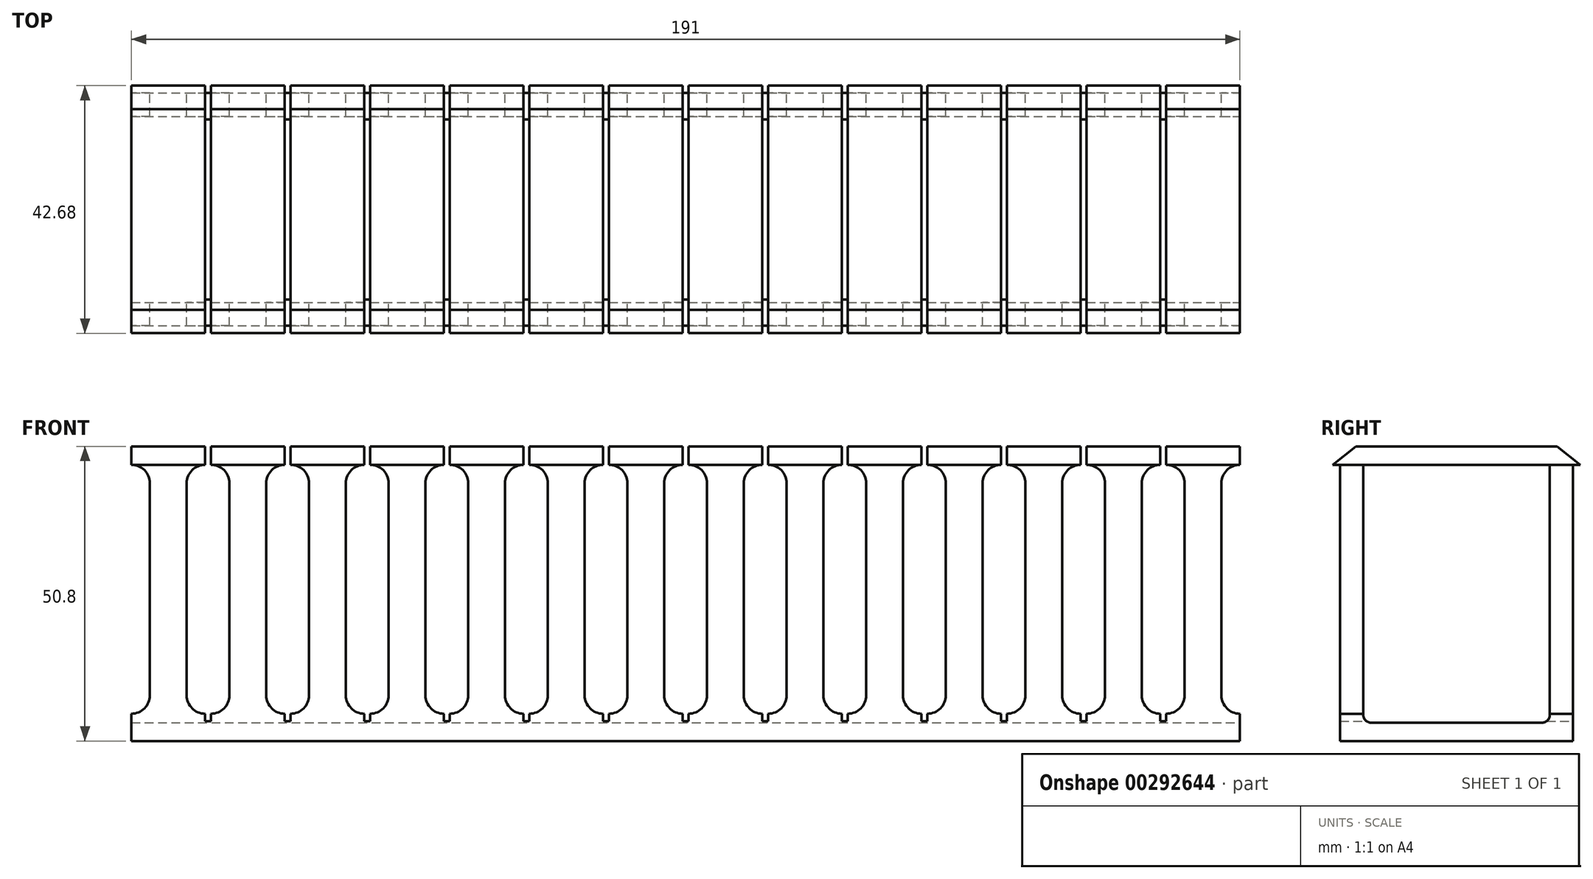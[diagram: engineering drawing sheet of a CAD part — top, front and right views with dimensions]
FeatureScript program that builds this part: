
annotation { "Feature Type Name" : "Feature", "Feature Type Description" : "" }
export const myFeature = defineFeature(function(context is Context, id is Id, definition is map)
    precondition{}
    {
        {
            var Q0;
            Q0=qCreatedBy(makeId("Front.planeOp"),FACE);
            var sketch = newSketch(context, id + "F0", { "sketchPlane" : qUnion([Q0])});
            skLineSegment(sketch, "E0.bottom", {"start": v(-95.5, 0) * mm, "end": v(95.5, 0) * mm});
            skLineSegment(sketch, "E0.top", {"start": v(-95.5, 50.8) * mm, "end": v(-82.8, 50.8) * mm});
            skLineSegment(sketch, "E0.left", {"start": v(-95.5, 0) * mm, "end": v(-95.5, 4.7) * mm});
            skLineSegment(sketch, "E0.right", {"start": v(95.5, 0) * mm, "end": v(95.5, 4.7) * mm});
            skLineSegment(sketch, "E1.trimOffspring", {"start": v(-95.5, 47.63) * mm, "end": v(-95.5, 50.8) * mm});
            skArc(sketch, "E2", {"start": v(-92.33, 44.45) * mm, "mid": v(-93.26, 46.7) * mm, "end": v(-95.5, 47.63) * mm});
            skArc(sketch, "E3", {"start": v(-95.5, 4.7) * mm, "mid": v(-93.26, 5.63) * mm, "end": v(-92.33, 7.87) * mm});
            skLineSegment(sketch, "E4", {"start": v(-92.33, 7.87) * mm, "end": v(-92.33, 44.45) * mm});
            skLineSegment(sketch, "E5", {"start": v(0, 0) * mm, "end": v(0, 0) * mm});
            skLineSegment(sketch, "E6.MirrorCS", {"start": v(95.5, 47.63) * mm, "end": v(95.5, 50.8) * mm});
            skLineSegment(sketch, "E7.MirrorCS", {"start": v(92.33, 7.87) * mm, "end": v(92.33, 44.45) * mm});
            skArc(sketch, "E8.MirrorCS", {"start": v(95.5, 4.7) * mm, "mid": v(93.26, 5.63) * mm, "end": v(92.33, 7.87) * mm});
            skArc(sketch, "E9", {"start": v(95.5, 47.63) * mm, "mid": v(93.26, 46.7) * mm, "end": v(92.33, 44.45) * mm});
            skLineSegment(sketch, "E10", {"start": v(-89.15, 50.8) * mm, "end": v(-89.15, 0) * mm, "construction": true});
            skArc(sketch, "E11.MirrorCS", {"start": v(-85.98, 44.45) * mm, "mid": v(-85.05, 46.7) * mm, "end": v(-82.8, 47.63) * mm});
            skLineSegment(sketch, "E12.MirrorCS", {"start": v(-82.8, 47.63) * mm, "end": v(-82.8, 50.8) * mm});
            skLineSegment(sketch, "E13.MirrorCS", {"start": v(-85.98, 7.87) * mm, "end": v(-85.98, 44.45) * mm});
            skArc(sketch, "E14.MirrorCS", {"start": v(-82.8, 4.7) * mm, "mid": v(-85.05, 5.63) * mm, "end": v(-85.98, 7.87) * mm});
            skLineSegment(sketch, "E15", {"start": v(-81.79, 50.8) * mm, "end": v(-69.09, 50.8) * mm});
            skLineSegment(sketch, "E16", {"start": v(-82.3, 50.8) * mm, "end": v(-82.3, 0) * mm, "construction": true});
            skArc(sketch, "E17.MirrorCS", {"start": v(-78.61, 44.45) * mm, "mid": v(-79.54, 46.7) * mm, "end": v(-81.79, 47.63) * mm});
            skLineSegment(sketch, "E18.MirrorCS", {"start": v(-81.79, 47.63) * mm, "end": v(-81.79, 50.8) * mm});
            skLineSegment(sketch, "E19.MirrorCS", {"start": v(-78.61, 7.87) * mm, "end": v(-78.61, 44.45) * mm});
            skArc(sketch, "E20.MirrorCS", {"start": v(-81.79, 4.7) * mm, "mid": v(-79.54, 5.63) * mm, "end": v(-78.61, 7.87) * mm});
            skLineSegment(sketch, "E21", {"start": v(-75.44, 50.8) * mm, "end": v(-75.44, 0) * mm, "construction": true});
            skLineSegment(sketch, "E22.MirrorCS", {"start": v(-69.09, 47.63) * mm, "end": v(-69.09, 50.8) * mm});
            skArc(sketch, "E23.MirrorCS", {"start": v(-72.26, 44.45) * mm, "mid": v(-71.33, 46.7) * mm, "end": v(-69.09, 47.63) * mm});
            skLineSegment(sketch, "E24.MirrorCS", {"start": v(-72.26, 7.87) * mm, "end": v(-72.26, 44.45) * mm});
            skArc(sketch, "E25.MirrorCS", {"start": v(-69.09, 4.7) * mm, "mid": v(-71.33, 5.63) * mm, "end": v(-72.26, 7.87) * mm});
            skLineSegment(sketch, "E26.MirrorCS", {"start": v(-68.07, 47.63) * mm, "end": v(-68.07, 50.8) * mm});
            skArc(sketch, "E27.MirrorCS", {"start": v(-64.9, 44.45) * mm, "mid": v(-65.83, 46.7) * mm, "end": v(-68.07, 47.63) * mm});
            skArc(sketch, "E28.MirrorCS", {"start": v(-68.07, 4.7) * mm, "mid": v(-65.83, 5.63) * mm, "end": v(-64.9, 7.87) * mm});
            skLineSegment(sketch, "E29.MirrorCS", {"start": v(-64.9, 7.87) * mm, "end": v(-64.9, 44.45) * mm});
            skLineSegment(sketch, "E30.MirrorCS", {"start": v(-58.55, 7.87) * mm, "end": v(-58.55, 44.45) * mm});
            skArc(sketch, "E31.MirrorCS", {"start": v(-58.55, 44.45) * mm, "mid": v(-57.62, 46.7) * mm, "end": v(-55.37, 47.63) * mm});
            skArc(sketch, "E32.MirrorCS", {"start": v(-55.37, 4.7) * mm, "mid": v(-57.62, 5.63) * mm, "end": v(-58.55, 7.87) * mm});
            skLineSegment(sketch, "E33", {"start": v(-68.07, 50.8) * mm, "end": v(-55.37, 50.8) * mm});
            skLineSegment(sketch, "E34", {"start": v(-61.72, 50.8) * mm, "end": v(-61.72, 0) * mm, "construction": true});
            skArc(sketch, "E35.MirrorCS", {"start": v(-51.18, 44.45) * mm, "mid": v(-52.11, 46.7) * mm, "end": v(-54.36, 47.63) * mm});
            skLineSegment(sketch, "E36.MirrorCS", {"start": v(-54.36, 47.63) * mm, "end": v(-54.36, 50.8) * mm});
            skLineSegment(sketch, "E37.MirrorCS", {"start": v(-55.37, 47.63) * mm, "end": v(-55.37, 50.8) * mm});
            skArc(sketch, "E38.MirrorCS", {"start": v(-54.36, 4.7) * mm, "mid": v(-52.11, 5.63) * mm, "end": v(-51.18, 7.87) * mm});
            skLineSegment(sketch, "E39.MirrorCS", {"start": v(-51.18, 7.87) * mm, "end": v(-51.18, 44.45) * mm});
            skLineSegment(sketch, "E40", {"start": v(-54.36, 50.8) * mm, "end": v(-41.66, 50.8) * mm});
            skLineSegment(sketch, "E41", {"start": v(-48, 50.8) * mm, "end": v(-48, 0) * mm, "construction": true});
            skLineSegment(sketch, "E42.MirrorCS", {"start": v(-68.58, 50.8) * mm, "end": v(-68.58, 0) * mm, "construction": true});
            skLineSegment(sketch, "E43.MirrorCS", {"start": v(-54.86, 50.8) * mm, "end": v(-54.86, 0) * mm, "construction": true});
            skLineSegment(sketch, "E44.MirrorCS", {"start": v(-44.83, 7.87) * mm, "end": v(-44.83, 44.45) * mm});
            skArc(sketch, "E45.MirrorCS", {"start": v(-44.83, 44.45) * mm, "mid": v(-43.9, 46.7) * mm, "end": v(-41.66, 47.63) * mm});
            skLineSegment(sketch, "E46.MirrorCS", {"start": v(-41.66, 47.63) * mm, "end": v(-41.66, 50.8) * mm});
            skLineSegment(sketch, "E47.MirrorCS", {"start": v(-41.15, 50.8) * mm, "end": v(-41.15, 0) * mm, "construction": true});
            skArc(sketch, "E48.MirrorCS", {"start": v(-41.66, 4.7) * mm, "mid": v(-43.9, 5.63) * mm, "end": v(-44.83, 7.87) * mm});
            skArc(sketch, "E49.MirrorCS", {"start": v(-37.46, 44.45) * mm, "mid": v(-38.4, 46.7) * mm, "end": v(-40.64, 47.63) * mm});
            skLineSegment(sketch, "E50.MirrorCS", {"start": v(-40.64, 47.63) * mm, "end": v(-40.64, 50.8) * mm});
            skLineSegment(sketch, "E51.MirrorCS", {"start": v(-37.47, 7.87) * mm, "end": v(-37.47, 44.45) * mm});
            skArc(sketch, "E52.MirrorCS", {"start": v(-40.64, 4.7) * mm, "mid": v(-38.4, 5.63) * mm, "end": v(-37.47, 7.87) * mm});
            skLineSegment(sketch, "E53.MirrorCS", {"start": v(-34.29, 50.8) * mm, "end": v(-34.3, 0) * mm, "construction": true});
            skLineSegment(sketch, "E54", {"start": v(-40.64, 50.8) * mm, "end": v(-27.94, 50.8) * mm});
            skLineSegment(sketch, "E55.MirrorCS", {"start": v(-27.94, 47.62) * mm, "end": v(-27.94, 50.8) * mm});
            skArc(sketch, "E56.MirrorCS", {"start": v(-31.12, 44.45) * mm, "mid": v(-30.19, 46.7) * mm, "end": v(-27.94, 47.62) * mm});
            skLineSegment(sketch, "E57.MirrorCS", {"start": v(-31.12, 7.87) * mm, "end": v(-31.11, 44.45) * mm});
            skArc(sketch, "E58.MirrorCS", {"start": v(-27.94, 4.7) * mm, "mid": v(-30.19, 5.63) * mm, "end": v(-31.11, 7.87) * mm});
            skLineSegment(sketch, "E59.MirrorCS", {"start": v(-27.43, 50.8) * mm, "end": v(-27.43, 0) * mm, "construction": true});
            skLineSegment(sketch, "E60.MirrorCS", {"start": v(-26.92, 47.62) * mm, "end": v(-26.92, 50.8) * mm});
            skArc(sketch, "E61.MirrorCS", {"start": v(-23.75, 44.45) * mm, "mid": v(-24.68, 46.7) * mm, "end": v(-26.92, 47.62) * mm});
            skLineSegment(sketch, "E62.MirrorCS", {"start": v(-23.75, 7.87) * mm, "end": v(-23.75, 44.45) * mm});
            skArc(sketch, "E63.MirrorCS", {"start": v(-26.92, 4.7) * mm, "mid": v(-24.68, 5.63) * mm, "end": v(-23.75, 7.87) * mm});
            skLineSegment(sketch, "E64", {"start": v(-26.92, 50.8) * mm, "end": v(-14.22, 50.8) * mm});
            skLineSegment(sketch, "E65", {"start": v(-20.57, 50.8) * mm, "end": v(-20.57, 0) * mm, "construction": true});
            skArc(sketch, "E66.MirrorCS", {"start": v(-17.4, 44.45) * mm, "mid": v(-16.47, 46.7) * mm, "end": v(-14.22, 47.62) * mm});
            skLineSegment(sketch, "E67.MirrorCS", {"start": v(-14.22, 47.62) * mm, "end": v(-14.22, 50.8) * mm});
            skLineSegment(sketch, "E68.MirrorCS", {"start": v(-17.4, 7.87) * mm, "end": v(-17.4, 44.45) * mm});
            skArc(sketch, "E69.MirrorCS", {"start": v(-14.22, 4.7) * mm, "mid": v(-16.47, 5.63) * mm, "end": v(-17.4, 7.87) * mm});
            skLineSegment(sketch, "E70.MirrorCS", {"start": v(-13.2, 47.62) * mm, "end": v(-13.2, 50.8) * mm});
            skArc(sketch, "E71.MirrorCS", {"start": v(-10.03, 44.45) * mm, "mid": v(-10.96, 46.7) * mm, "end": v(-13.2, 47.62) * mm});
            skLineSegment(sketch, "E72.MirrorCS", {"start": v(-10.03, 7.87) * mm, "end": v(-10.03, 44.45) * mm});
            skArc(sketch, "E73.MirrorCS", {"start": v(-13.2, 4.7) * mm, "mid": v(-10.96, 5.63) * mm, "end": v(-10.03, 7.87) * mm});
            skLineSegment(sketch, "E74.MirrorCS", {"start": v(-13.72, 50.8) * mm, "end": v(-13.72, 0) * mm, "construction": true});
            skLineSegment(sketch, "E75", {"start": v(-13.2, 50.8) * mm, "end": v(-0.5, 50.8) * mm});
            skLineSegment(sketch, "E76", {"start": v(-6.86, 50.8) * mm, "end": v(-6.86, 0) * mm, "construction": true});
            skArc(sketch, "E77.MirrorCS", {"start": v(-3.68, 44.45) * mm, "mid": v(-2.75, 46.7) * mm, "end": v(-0.5, 47.62) * mm});
            skLineSegment(sketch, "E78.MirrorCS", {"start": v(-3.68, 7.87) * mm, "end": v(-3.68, 44.45) * mm});
            skLineSegment(sketch, "E79.MirrorCS", {"start": v(-0.5, 47.62) * mm, "end": v(-0.5, 50.8) * mm});
            skArc(sketch, "E80.MirrorCS", {"start": v(-0.5, 4.7) * mm, "mid": v(-2.75, 5.63) * mm, "end": v(-3.68, 7.87) * mm});
            skLineSegment(sketch, "E81.MirrorCS", {"start": v(3.68, 7.87) * mm, "end": v(3.68, 44.45) * mm});
            skArc(sketch, "E82.MirrorCS", {"start": v(0.5, 4.7) * mm, "mid": v(2.75, 5.63) * mm, "end": v(3.68, 7.87) * mm});
            skArc(sketch, "E83.MirrorCS", {"start": v(3.68, 44.45) * mm, "mid": v(2.75, 46.7) * mm, "end": v(0.5, 47.62) * mm});
            skLineSegment(sketch, "E84.MirrorCS", {"start": v(0.5, 47.62) * mm, "end": v(0.5, 50.8) * mm});
            skLineSegment(sketch, "E85.MirrorCS", {"start": v(0, 50.8) * mm, "end": v(0, 0) * mm, "construction": true});
            skLineSegment(sketch, "E86", {"start": v(0.5, 50.8) * mm, "end": v(13.2, 50.8) * mm});
            skLineSegment(sketch, "E87", {"start": v(6.86, 50.8) * mm, "end": v(6.86, 0) * mm, "construction": true});
            skArc(sketch, "E88.MirrorCS", {"start": v(10.03, 44.45) * mm, "mid": v(10.96, 46.7) * mm, "end": v(13.2, 47.62) * mm});
            skLineSegment(sketch, "E89.MirrorCS", {"start": v(13.2, 47.62) * mm, "end": v(13.2, 50.8) * mm});
            skArc(sketch, "E90.MirrorCS", {"start": v(13.2, 4.7) * mm, "mid": v(10.96, 5.63) * mm, "end": v(10.03, 7.87) * mm});
            skLineSegment(sketch, "E91.MirrorCS", {"start": v(13.72, 50.8) * mm, "end": v(13.72, 0) * mm, "construction": true});
            skLineSegment(sketch, "E92.MirrorCS", {"start": v(17.4, 7.87) * mm, "end": v(17.4, 44.45) * mm});
            skArc(sketch, "E93.MirrorCS", {"start": v(14.22, 4.7) * mm, "mid": v(16.47, 5.63) * mm, "end": v(17.4, 7.87) * mm});
            skArc(sketch, "E94.MirrorCS", {"start": v(17.4, 44.45) * mm, "mid": v(16.47, 46.7) * mm, "end": v(14.22, 47.62) * mm});
            skLineSegment(sketch, "E95.MirrorCS", {"start": v(10.03, 7.87) * mm, "end": v(10.03, 44.45) * mm});
            skLineSegment(sketch, "E96.MirrorCS", {"start": v(14.22, 47.62) * mm, "end": v(14.22, 50.8) * mm});
            skLineSegment(sketch, "E97", {"start": v(14.22, 50.8) * mm, "end": v(26.92, 50.8) * mm});
            skLineSegment(sketch, "E98", {"start": v(20.57, 50.8) * mm, "end": v(20.57, 0) * mm, "construction": true});
            skArc(sketch, "E99.MirrorCS", {"start": v(26.92, 4.7) * mm, "mid": v(24.68, 5.63) * mm, "end": v(23.75, 7.87) * mm});
            skArc(sketch, "E100.MirrorCS", {"start": v(27.94, 4.7) * mm, "mid": v(30.19, 5.63) * mm, "end": v(31.11, 7.87) * mm});
            skLineSegment(sketch, "E101.MirrorCS", {"start": v(31.11, 7.87) * mm, "end": v(31.11, 44.45) * mm});
            skLineSegment(sketch, "E102.MirrorCS", {"start": v(27.43, 50.8) * mm, "end": v(27.43, 0) * mm, "construction": true});
            skLineSegment(sketch, "E103.MirrorCS", {"start": v(23.75, 7.87) * mm, "end": v(23.75, 44.45) * mm});
            skArc(sketch, "E104.MirrorCS", {"start": v(23.75, 44.45) * mm, "mid": v(24.68, 46.7) * mm, "end": v(26.92, 47.62) * mm});
            skLineSegment(sketch, "E105.MirrorCS", {"start": v(26.92, 47.62) * mm, "end": v(26.92, 50.8) * mm});
            skLineSegment(sketch, "E106.MirrorCS", {"start": v(27.94, 47.62) * mm, "end": v(27.94, 50.8) * mm});
            skArc(sketch, "E107.MirrorCS", {"start": v(31.11, 44.45) * mm, "mid": v(30.19, 46.7) * mm, "end": v(27.94, 47.62) * mm});
            skLineSegment(sketch, "E108", {"start": v(27.94, 50.8) * mm, "end": v(40.64, 50.8) * mm});
            skLineSegment(sketch, "E109", {"start": v(34.29, 50.8) * mm, "end": v(34.29, 0) * mm, "construction": true});
            skArc(sketch, "E110.MirrorCS", {"start": v(40.64, 4.7) * mm, "mid": v(38.4, 5.63) * mm, "end": v(37.47, 7.87) * mm});
            skLineSegment(sketch, "E111.MirrorCS", {"start": v(37.47, 7.87) * mm, "end": v(37.47, 44.45) * mm});
            skArc(sketch, "E112.MirrorCS", {"start": v(37.46, 44.45) * mm, "mid": v(38.4, 46.7) * mm, "end": v(40.64, 47.62) * mm});
            skLineSegment(sketch, "E113.MirrorCS", {"start": v(40.64, 47.62) * mm, "end": v(40.64, 50.8) * mm});
            skLineSegment(sketch, "E114.MirrorCS", {"start": v(41.15, 50.8) * mm, "end": v(41.15, 0) * mm, "construction": true});
            skLineSegment(sketch, "E115.MirrorCS", {"start": v(41.66, 47.62) * mm, "end": v(41.66, 50.8) * mm});
            skArc(sketch, "E116.MirrorCS", {"start": v(44.83, 44.45) * mm, "mid": v(43.9, 46.7) * mm, "end": v(41.66, 47.62) * mm});
            skLineSegment(sketch, "E117.MirrorCS", {"start": v(44.83, 7.87) * mm, "end": v(44.83, 44.45) * mm});
            skArc(sketch, "E118.MirrorCS", {"start": v(41.66, 4.7) * mm, "mid": v(43.9, 5.63) * mm, "end": v(44.83, 7.87) * mm});
            skLineSegment(sketch, "E119", {"start": v(41.66, 50.8) * mm, "end": v(54.36, 50.8) * mm});
            skLineSegment(sketch, "E120", {"start": v(48, 50.8) * mm, "end": v(48, 0) * mm, "construction": true});
            skLineSegment(sketch, "E121.MirrorCS", {"start": v(51.18, 7.87) * mm, "end": v(51.18, 44.45) * mm});
            skArc(sketch, "E122.MirrorCS", {"start": v(51.18, 44.45) * mm, "mid": v(52.11, 46.7) * mm, "end": v(54.36, 47.62) * mm});
            skLineSegment(sketch, "E123.MirrorCS", {"start": v(54.36, 47.62) * mm, "end": v(54.36, 50.8) * mm});
            skLineSegment(sketch, "E124.MirrorCS", {"start": v(54.86, 50.8) * mm, "end": v(54.86, 0) * mm, "construction": true});
            skLineSegment(sketch, "E125.MirrorCS", {"start": v(55.37, 47.62) * mm, "end": v(55.37, 50.8) * mm});
            skArc(sketch, "E126.MirrorCS", {"start": v(58.55, 44.45) * mm, "mid": v(57.62, 46.7) * mm, "end": v(55.37, 47.62) * mm});
            skLineSegment(sketch, "E127.MirrorCS", {"start": v(58.55, 7.87) * mm, "end": v(58.55, 44.45) * mm});
            skArc(sketch, "E128.MirrorCS", {"start": v(55.37, 4.7) * mm, "mid": v(57.62, 5.63) * mm, "end": v(58.55, 7.87) * mm});
            skArc(sketch, "E129.MirrorCS", {"start": v(54.36, 4.7) * mm, "mid": v(52.11, 5.63) * mm, "end": v(51.18, 7.87) * mm});
            skLineSegment(sketch, "E130", {"start": v(55.37, 50.8) * mm, "end": v(68.07, 50.8) * mm});
            skLineSegment(sketch, "E131", {"start": v(61.72, 50.8) * mm, "end": v(61.72, 0) * mm, "construction": true});
            skLineSegment(sketch, "E132.MirrorCS", {"start": v(64.9, 7.87) * mm, "end": v(64.9, 44.45) * mm});
            skArc(sketch, "E133.MirrorCS", {"start": v(64.9, 44.45) * mm, "mid": v(65.83, 46.7) * mm, "end": v(68.07, 47.63) * mm});
            skLineSegment(sketch, "E134.MirrorCS", {"start": v(68.07, 47.63) * mm, "end": v(68.07, 50.8) * mm});
            skArc(sketch, "E135.MirrorCS", {"start": v(68.07, 4.7) * mm, "mid": v(65.83, 5.63) * mm, "end": v(64.9, 7.87) * mm});
            skLineSegment(sketch, "E136.MirrorCS", {"start": v(68.58, 50.8) * mm, "end": v(68.58, 0) * mm, "construction": true});
            skLineSegment(sketch, "E137.MirrorCS", {"start": v(72.26, 7.87) * mm, "end": v(72.26, 44.45) * mm});
            skArc(sketch, "E138.MirrorCS", {"start": v(69.09, 4.7) * mm, "mid": v(71.33, 5.63) * mm, "end": v(72.26, 7.87) * mm});
            skArc(sketch, "E139.MirrorCS", {"start": v(72.26, 44.45) * mm, "mid": v(71.33, 46.7) * mm, "end": v(69.09, 47.63) * mm});
            skLineSegment(sketch, "E140.MirrorCS", {"start": v(69.09, 47.63) * mm, "end": v(69.09, 50.8) * mm});
            skLineSegment(sketch, "E141", {"start": v(69.09, 50.8) * mm, "end": v(81.79, 50.8) * mm});
            skLineSegment(sketch, "E142", {"start": v(75.44, 50.8) * mm, "end": v(75.44, 0) * mm, "construction": true});
            skLineSegment(sketch, "E143.MirrorCS", {"start": v(78.61, 7.87) * mm, "end": v(78.61, 44.45) * mm});
            skArc(sketch, "E144.MirrorCS", {"start": v(78.61, 44.45) * mm, "mid": v(79.54, 46.7) * mm, "end": v(81.79, 47.63) * mm});
            skLineSegment(sketch, "E145.MirrorCS", {"start": v(81.79, 47.63) * mm, "end": v(81.79, 50.8) * mm});
            skArc(sketch, "E146.MirrorCS", {"start": v(81.79, 4.7) * mm, "mid": v(79.54, 5.63) * mm, "end": v(78.61, 7.87) * mm});
            skLineSegment(sketch, "E147.MirrorCS", {"start": v(82.3, 50.8) * mm, "end": v(82.3, 0) * mm, "construction": true});
            skLineSegment(sketch, "E148.MirrorCS", {"start": v(85.98, 7.87) * mm, "end": v(85.98, 44.45) * mm});
            skArc(sketch, "E149.MirrorCS", {"start": v(82.8, 4.7) * mm, "mid": v(85.05, 5.63) * mm, "end": v(85.98, 7.87) * mm});
            skArc(sketch, "E150.MirrorCS", {"start": v(85.98, 44.45) * mm, "mid": v(85.05, 46.7) * mm, "end": v(82.8, 47.63) * mm});
            skLineSegment(sketch, "E151.MirrorCS", {"start": v(82.8, 47.63) * mm, "end": v(82.8, 50.8) * mm});
            skLineSegment(sketch, "E152", {"start": v(-0.5, 4.7) * mm, "end": v(-0.5, 3.43) * mm});
            skLineSegment(sketch, "E153", {"start": v(-0.5, 3.43) * mm, "end": v(0.5, 3.43) * mm});
            skLineSegment(sketch, "E154", {"start": v(0.5, 3.43) * mm, "end": v(0.5, 4.7) * mm});
            skLineSegment(sketch, "E155.MirrorCS", {"start": v(13.2, 3.43) * mm, "end": v(13.2, 4.7) * mm});
            skLineSegment(sketch, "E156.MirrorCS", {"start": v(14.22, 3.43) * mm, "end": v(13.2, 3.43) * mm});
            skLineSegment(sketch, "E157.MirrorCS", {"start": v(14.22, 4.7) * mm, "end": v(14.22, 3.43) * mm});
            skLineSegment(sketch, "E158.MirrorCS", {"start": v(26.92, 3.43) * mm, "end": v(27.94, 3.43) * mm});
            skLineSegment(sketch, "E159.MirrorCS", {"start": v(26.92, 4.7) * mm, "end": v(26.92, 3.43) * mm});
            skLineSegment(sketch, "E160.MirrorCS", {"start": v(27.94, 3.43) * mm, "end": v(27.94, 4.7) * mm});
            skLineSegment(sketch, "E161.MirrorCS", {"start": v(55.37, 3.43) * mm, "end": v(54.36, 3.43) * mm});
            skLineSegment(sketch, "E162.MirrorCS", {"start": v(54.36, 3.43) * mm, "end": v(54.36, 4.7) * mm});
            skLineSegment(sketch, "E163.MirrorCS", {"start": v(55.37, 4.7) * mm, "end": v(55.37, 3.43) * mm});
            skLineSegment(sketch, "E164.MirrorCS", {"start": v(41.66, 4.7) * mm, "end": v(41.66, 3.43) * mm});
            skLineSegment(sketch, "E165.MirrorCS", {"start": v(40.64, 3.43) * mm, "end": v(40.64, 4.7) * mm});
            skLineSegment(sketch, "E166.MirrorCS", {"start": v(41.66, 3.43) * mm, "end": v(40.64, 3.43) * mm});
            skLineSegment(sketch, "E167.MirrorCS", {"start": v(68.07, 4.7) * mm, "end": v(68.07, 3.43) * mm});
            skLineSegment(sketch, "E168.MirrorCS", {"start": v(68.07, 3.43) * mm, "end": v(69.09, 3.43) * mm});
            skLineSegment(sketch, "E169.MirrorCS", {"start": v(69.09, 3.43) * mm, "end": v(69.09, 4.7) * mm});
            skLineSegment(sketch, "E170.MirrorCS", {"start": v(81.79, 3.43) * mm, "end": v(81.79, 4.7) * mm});
            skLineSegment(sketch, "E171.MirrorCS", {"start": v(82.8, 3.43) * mm, "end": v(81.79, 3.43) * mm});
            skLineSegment(sketch, "E172.MirrorCS", {"start": v(82.8, 4.7) * mm, "end": v(82.8, 3.43) * mm});
            skLineSegment(sketch, "E173.MirrorCS", {"start": v(-14.22, 3.43) * mm, "end": v(-14.22, 4.7) * mm});
            skLineSegment(sketch, "E174.MirrorCS", {"start": v(-13.2, 3.43) * mm, "end": v(-14.22, 3.43) * mm});
            skLineSegment(sketch, "E175.MirrorCS", {"start": v(-13.2, 4.7) * mm, "end": v(-13.2, 3.43) * mm});
            skLineSegment(sketch, "E176.MirrorCS", {"start": v(-26.92, 3.43) * mm, "end": v(-26.92, 4.7) * mm});
            skLineSegment(sketch, "E177.MirrorCS", {"start": v(-27.94, 4.7) * mm, "end": v(-27.94, 3.43) * mm});
            skLineSegment(sketch, "E178.MirrorCS", {"start": v(-27.94, 3.43) * mm, "end": v(-26.92, 3.43) * mm});
            skLineSegment(sketch, "E179.MirrorCS", {"start": v(-41.66, 3.43) * mm, "end": v(-41.66, 4.7) * mm});
            skLineSegment(sketch, "E180.MirrorCS", {"start": v(-40.64, 3.43) * mm, "end": v(-41.66, 3.43) * mm});
            skLineSegment(sketch, "E181.MirrorCS", {"start": v(-40.64, 4.7) * mm, "end": v(-40.64, 3.43) * mm});
            skLineSegment(sketch, "E182.MirrorCS", {"start": v(-54.36, 3.43) * mm, "end": v(-54.36, 4.7) * mm});
            skLineSegment(sketch, "E183", {"start": v(-55.37, 4.7) * mm, "end": v(-55.37, 3.43) * mm});
            skLineSegment(sketch, "E184", {"start": v(-55.37, 3.43) * mm, "end": v(-54.36, 3.43) * mm});
            skLineSegment(sketch, "E185.MirrorCS", {"start": v(-69.09, 3.43) * mm, "end": v(-69.09, 4.7) * mm});
            skLineSegment(sketch, "E186.MirrorCS", {"start": v(-68.07, 3.43) * mm, "end": v(-69.09, 3.43) * mm});
            skLineSegment(sketch, "E187.MirrorCS", {"start": v(-68.07, 4.7) * mm, "end": v(-68.07, 3.43) * mm});
            skLineSegment(sketch, "E188.MirrorCS", {"start": v(-81.79, 3.43) * mm, "end": v(-81.79, 4.7) * mm});
            skLineSegment(sketch, "E189.MirrorCS", {"start": v(-82.8, 4.7) * mm, "end": v(-82.8, 3.43) * mm});
            skLineSegment(sketch, "E190.MirrorCS", {"start": v(-82.8, 3.43) * mm, "end": v(-81.79, 3.43) * mm});
            skLineSegment(sketch, "E191.trimOffspring", {"start": v(-54.36, 50.8) * mm, "end": v(-48, 50.8) * mm});
            skLineSegment(sketch, "E192.trimOffspring", {"start": v(82.8, 50.8) * mm, "end": v(95.5, 50.8) * mm});
            skLineSegment(sketch, "E193.trimOffspring", {"start": v(41.15, 50.8) * mm, "end": v(48, 50.8) * mm});
            skLineSegment(sketch, "E194.trimOffspring", {"start": v(27.94, 50.8) * mm, "end": v(34.29, 50.8) * mm});
            skSolve(sketch);
        }
        {
            var Q0;
            Q0 = qSketchRegion(id + "F0", true);
            extrude(context, id + "F1", {"entities" : qUnion([Q0]), "depth" : 42.67 * mm, "symmetric" : true});
        }
        {
            var Q0;
            Q0=makeQuery(id+"F1.opExtrude","SWEPT_FACE",FACE,{"disambiguationData":[OSD([sQuery(id+"F0.wireOp",EDGE,"E6.MirrorCS")])]});
            var sketch = newSketch(context, id + "F2", { "sketchPlane" : qUnion([Q0])});
            skLineSegment(sketch, "E195", {"start": v(-21.34, 50.8) * mm, "end": v(21.34, 50.8) * mm});
            skLineSegment(sketch, "E196", {"start": v(21.34, 50.8) * mm, "end": v(21.34, 0) * mm});
            skLineSegment(sketch, "E197", {"start": v(21.34, 0) * mm, "end": v(-21.34, 0) * mm});
            skLineSegment(sketch, "E198", {"start": v(-21.34, 0) * mm, "end": v(-21.34, 50.8) * mm});
            skLineSegment(sketch, "E199", {"start": v(21.34, 50.8) * mm, "end": v(18.7, 50.8) * mm});
            skLineSegment(sketch, "E200", {"start": v(0, 55.4) * mm, "end": v(0, -7.26) * mm, "construction": true});
            skLineSegment(sketch, "E201.MirrorCS", {"start": v(-21.34, 50.8) * mm, "end": v(-18.7, 50.8) * mm});
            skLineSegment(sketch, "E202", {"start": v(24.79, 0) * mm, "end": v(24.79, 3.18) * mm});
            skLineSegment(sketch, "E203", {"start": v(16.05, 50.8) * mm, "end": v(16.05, 3.18) * mm});
            skLineSegment(sketch, "E204", {"start": v(16.05, 3.18) * mm, "end": v(-16.05, 3.17) * mm});
            skLineSegment(sketch, "E205", {"start": v(-16.05, 3.17) * mm, "end": v(-16.05, 50.8) * mm});
            skLineSegment(sketch, "E206", {"start": v(-16.05, 50.8) * mm, "end": v(16.05, 50.8) * mm});
            skSolve(sketch);
        }
        {
            var Q0;
            {var subQ0=sQuery(id+"F2.wireOp",EDGE,"E204");Q0=makeQuery(id+"F2.imprint","IMPRINT",FACE,{"disambiguationData":[TD([[makeQuery(id+"F2.imprint","IMPRINT",EDGE,{"derivedFrom":subQ0}),-1.0]])]});}
            var Q1;
            {var subQ0=sQuery(id+"F2.wireOp",EDGE,"E206");Q1=makeQuery(id+"F2.imprint","IMPRINT",FACE,{"disambiguationData":[TD([[makeQuery(id+"F2.imprint","IMPRINT",EDGE,{"derivedFrom":subQ0}),-1.0]])]});}
            extrude(context, id + "F3", {"entities" : qUnion([Q0, Q1]), "operationType" : NewBodyOperationType.REMOVE, "endBound" : BoundingType.THROUGH_ALL, "oppositeDirection" : true, "depth" : 25.4 * mm});
        }
        {
            var Q0;
            Q0=qCreatedBy(makeId("Right.planeOp"),FACE);
            var sketch = newSketch(context, id + "F4", { "sketchPlane" : qUnion([Q0])});
            skLineSegment(sketch, "E207", {"start": v(0, -5.93) * mm, "end": v(0, 55.46) * mm, "construction": true});
            skSolve(sketch);
        }
        {
            var Q0;
            {var subQ0=sQuery(id+"F2.wireOp",EDGE,"E203");Q0=makeQuery(id+"F3.boolean.opBoolean","COPY",EDGE,{"disambiguationData":[topologyDisambiguationEdgeConnected([makeQuery(id+"F1.opExtrude","SWEPT_FACE",FACE,{"disambiguationData":[OSD([sQuery(id+"F0.wireOp",EDGE,"E0.top")])]})])],"derivedFrom":makeQuery(id+"F3.opExtrude","SWEPT_EDGE",EDGE,{"disambiguationData":[OSD([sQuery(id+"F2.wireOp",EDGE,"E195"),subQ0,sQuery(id+"F2.wireOp",EDGE,"E206")])]})});}
            var Q1;
            {var subQ0=sQuery(id+"F2.wireOp",EDGE,"E203");Q1=makeQuery(id+"F3.boolean.opBoolean","COPY",EDGE,{"disambiguationData":[topologyDisambiguationEdgeConnected([makeQuery(id+"F1.opExtrude","SWEPT_FACE",FACE,{"disambiguationData":[OSD([sQuery(id+"F0.wireOp",EDGE,"E15")])]})])],"derivedFrom":makeQuery(id+"F3.opExtrude","SWEPT_EDGE",EDGE,{"disambiguationData":[OSD([sQuery(id+"F2.wireOp",EDGE,"E195"),subQ0,sQuery(id+"F2.wireOp",EDGE,"E206")])]})});}
            var Q2;
            {var subQ0=sQuery(id+"F2.wireOp",EDGE,"E203");Q2=makeQuery(id+"F3.boolean.opBoolean","COPY",EDGE,{"disambiguationData":[topologyDisambiguationEdgeConnected([makeQuery(id+"F1.opExtrude","SWEPT_FACE",FACE,{"disambiguationData":[OSD([sQuery(id+"F0.wireOp",EDGE,"E33")])]})])],"derivedFrom":makeQuery(id+"F3.opExtrude","SWEPT_EDGE",EDGE,{"disambiguationData":[OSD([sQuery(id+"F2.wireOp",EDGE,"E195"),subQ0,sQuery(id+"F2.wireOp",EDGE,"E206")])]})});}
            var Q3;
            {var subQ0=sQuery(id+"F2.wireOp",EDGE,"E203");Q3=makeQuery(id+"F3.boolean.opBoolean","COPY",EDGE,{"disambiguationData":[topologyDisambiguationEdgeConnected([makeQuery(id+"F1.opExtrude","SWEPT_FACE",FACE,{"disambiguationData":[OSD([sQuery(id+"F0.wireOp",EDGE,"E40"),sQuery(id+"F0.wireOp",EDGE,"E191.trimOffspring")])]})])],"derivedFrom":makeQuery(id+"F3.opExtrude","SWEPT_EDGE",EDGE,{"disambiguationData":[OSD([sQuery(id+"F2.wireOp",EDGE,"E195"),subQ0,sQuery(id+"F2.wireOp",EDGE,"E206")])]})});}
            var Q4;
            {var subQ0=sQuery(id+"F2.wireOp",EDGE,"E203");Q4=makeQuery(id+"F3.boolean.opBoolean","COPY",EDGE,{"disambiguationData":[topologyDisambiguationEdgeConnected([makeQuery(id+"F1.opExtrude","SWEPT_FACE",FACE,{"disambiguationData":[OSD([sQuery(id+"F0.wireOp",EDGE,"E54")])]})])],"derivedFrom":makeQuery(id+"F3.opExtrude","SWEPT_EDGE",EDGE,{"disambiguationData":[OSD([sQuery(id+"F2.wireOp",EDGE,"E195"),subQ0,sQuery(id+"F2.wireOp",EDGE,"E206")])]})});}
            var Q5;
            {var subQ0=sQuery(id+"F2.wireOp",EDGE,"E203");Q5=makeQuery(id+"F3.boolean.opBoolean","COPY",EDGE,{"disambiguationData":[topologyDisambiguationEdgeConnected([makeQuery(id+"F1.opExtrude","SWEPT_FACE",FACE,{"disambiguationData":[OSD([sQuery(id+"F0.wireOp",EDGE,"E75")])]})])],"derivedFrom":makeQuery(id+"F3.opExtrude","SWEPT_EDGE",EDGE,{"disambiguationData":[OSD([sQuery(id+"F2.wireOp",EDGE,"E195"),subQ0,sQuery(id+"F2.wireOp",EDGE,"E206")])]})});}
            var Q6;
            {var subQ0=sQuery(id+"F2.wireOp",EDGE,"E203");Q6=makeQuery(id+"F3.boolean.opBoolean","COPY",EDGE,{"disambiguationData":[topologyDisambiguationEdgeConnected([makeQuery(id+"F1.opExtrude","SWEPT_FACE",FACE,{"disambiguationData":[OSD([sQuery(id+"F0.wireOp",EDGE,"E86")])]})])],"derivedFrom":makeQuery(id+"F3.opExtrude","SWEPT_EDGE",EDGE,{"disambiguationData":[OSD([sQuery(id+"F2.wireOp",EDGE,"E195"),subQ0,sQuery(id+"F2.wireOp",EDGE,"E206")])]})});}
            var Q7;
            {var subQ0=sQuery(id+"F2.wireOp",EDGE,"E203");Q7=makeQuery(id+"F3.boolean.opBoolean","COPY",EDGE,{"disambiguationData":[topologyDisambiguationEdgeConnected([makeQuery(id+"F1.opExtrude","SWEPT_FACE",FACE,{"disambiguationData":[OSD([sQuery(id+"F0.wireOp",EDGE,"E97")])]})])],"derivedFrom":makeQuery(id+"F3.opExtrude","SWEPT_EDGE",EDGE,{"disambiguationData":[OSD([sQuery(id+"F2.wireOp",EDGE,"E195"),subQ0,sQuery(id+"F2.wireOp",EDGE,"E206")])]})});}
            var Q8;
            {var subQ0=sQuery(id+"F2.wireOp",EDGE,"E203");Q8=makeQuery(id+"F3.boolean.opBoolean","COPY",EDGE,{"disambiguationData":[topologyDisambiguationEdgeConnected([makeQuery(id+"F1.opExtrude","SWEPT_FACE",FACE,{"disambiguationData":[OSD([sQuery(id+"F0.wireOp",EDGE,"E108"),sQuery(id+"F0.wireOp",EDGE,"E194.trimOffspring")])]})])],"derivedFrom":makeQuery(id+"F3.opExtrude","SWEPT_EDGE",EDGE,{"disambiguationData":[OSD([sQuery(id+"F2.wireOp",EDGE,"E195"),subQ0,sQuery(id+"F2.wireOp",EDGE,"E206")])]})});}
            var Q9;
            {var subQ0=sQuery(id+"F2.wireOp",EDGE,"E203");Q9=makeQuery(id+"F3.boolean.opBoolean","COPY",EDGE,{"disambiguationData":[topologyDisambiguationEdgeConnected([makeQuery(id+"F1.opExtrude","SWEPT_FACE",FACE,{"disambiguationData":[OSD([sQuery(id+"F0.wireOp",EDGE,"E119"),sQuery(id+"F0.wireOp",EDGE,"E193.trimOffspring")])]})])],"derivedFrom":makeQuery(id+"F3.opExtrude","SWEPT_EDGE",EDGE,{"disambiguationData":[OSD([sQuery(id+"F2.wireOp",EDGE,"E195"),subQ0,sQuery(id+"F2.wireOp",EDGE,"E206")])]})});}
            var Q10;
            {var subQ0=sQuery(id+"F2.wireOp",EDGE,"E203");Q10=makeQuery(id+"F3.boolean.opBoolean","COPY",EDGE,{"disambiguationData":[topologyDisambiguationEdgeConnected([makeQuery(id+"F1.opExtrude","SWEPT_FACE",FACE,{"disambiguationData":[OSD([sQuery(id+"F0.wireOp",EDGE,"E130")])]})])],"derivedFrom":makeQuery(id+"F3.opExtrude","SWEPT_EDGE",EDGE,{"disambiguationData":[OSD([sQuery(id+"F2.wireOp",EDGE,"E195"),subQ0,sQuery(id+"F2.wireOp",EDGE,"E206")])]})});}
            var Q11;
            {var subQ0=sQuery(id+"F2.wireOp",EDGE,"E203");Q11=makeQuery(id+"F3.boolean.opBoolean","COPY",EDGE,{"disambiguationData":[topologyDisambiguationEdgeConnected([makeQuery(id+"F1.opExtrude","SWEPT_FACE",FACE,{"disambiguationData":[OSD([sQuery(id+"F0.wireOp",EDGE,"E141")])]})])],"derivedFrom":makeQuery(id+"F3.opExtrude","SWEPT_EDGE",EDGE,{"disambiguationData":[OSD([sQuery(id+"F2.wireOp",EDGE,"E195"),subQ0,sQuery(id+"F2.wireOp",EDGE,"E206")])]})});}
            var Q12;
            {var subQ0=sQuery(id+"F2.wireOp",EDGE,"E203");Q12=makeQuery(id+"F3.boolean.opBoolean","COPY",EDGE,{"disambiguationData":[topologyDisambiguationEdgeConnected([makeQuery(id+"F1.opExtrude","SWEPT_FACE",FACE,{"disambiguationData":[OSD([sQuery(id+"F0.wireOp",EDGE,"E192.trimOffspring")])]})])],"derivedFrom":makeQuery(id+"F3.opExtrude","SWEPT_EDGE",EDGE,{"disambiguationData":[OSD([sQuery(id+"F2.wireOp",EDGE,"E195"),subQ0,sQuery(id+"F2.wireOp",EDGE,"E206")])]})});}
            var Q13;
            {var subQ0=sQuery(id+"F2.wireOp",EDGE,"E203");Q13=makeQuery(id+"F3.boolean.opBoolean","COPY",EDGE,{"disambiguationData":[topologyDisambiguationEdgeConnected([makeQuery(id+"F1.opExtrude","SWEPT_FACE",FACE,{"disambiguationData":[OSD([sQuery(id+"F0.wireOp",EDGE,"E64")])]})])],"derivedFrom":makeQuery(id+"F3.opExtrude","SWEPT_EDGE",EDGE,{"disambiguationData":[OSD([sQuery(id+"F2.wireOp",EDGE,"E195"),subQ0,sQuery(id+"F2.wireOp",EDGE,"E206")])]})});}
            fillet(context, id + "F5", {"entities" : qUnion([Q0, Q1, Q2, Q3, Q4, Q5, Q6, Q7, Q8, Q9, Q10, Q11, Q12, Q13]), "radius" : 1.27 * mm, "tangentPropagation" : true, "allowEdgeOverflow" : false});
        }
        {
            var Q0;
            {var subQ0=sQuery(id+"F2.wireOp",EDGE,"E205");Q0=makeQuery(id+"F3.boolean.opBoolean","COPY",EDGE,{"disambiguationData":[topologyDisambiguationEdgeConnected([makeQuery(id+"F1.opExtrude","SWEPT_FACE",FACE,{"disambiguationData":[OSD([sQuery(id+"F0.wireOp",EDGE,"E0.top")])]})])],"derivedFrom":makeQuery(id+"F3.opExtrude","SWEPT_EDGE",EDGE,{"disambiguationData":[OSD([sQuery(id+"F2.wireOp",EDGE,"E195"),subQ0,sQuery(id+"F2.wireOp",EDGE,"E206")])]})});}
            var Q1;
            {var subQ0=sQuery(id+"F2.wireOp",EDGE,"E205");Q1=makeQuery(id+"F3.boolean.opBoolean","COPY",EDGE,{"disambiguationData":[topologyDisambiguationEdgeConnected([makeQuery(id+"F1.opExtrude","SWEPT_FACE",FACE,{"disambiguationData":[OSD([sQuery(id+"F0.wireOp",EDGE,"E192.trimOffspring")])]})])],"derivedFrom":makeQuery(id+"F3.opExtrude","SWEPT_EDGE",EDGE,{"disambiguationData":[OSD([sQuery(id+"F2.wireOp",EDGE,"E195"),subQ0,sQuery(id+"F2.wireOp",EDGE,"E206")])]})});}
            var Q2;
            {var subQ0=sQuery(id+"F2.wireOp",EDGE,"E205");Q2=makeQuery(id+"F3.boolean.opBoolean","COPY",EDGE,{"disambiguationData":[topologyDisambiguationEdgeConnected([makeQuery(id+"F1.opExtrude","SWEPT_FACE",FACE,{"disambiguationData":[OSD([sQuery(id+"F0.wireOp",EDGE,"E141")])]})])],"derivedFrom":makeQuery(id+"F3.opExtrude","SWEPT_EDGE",EDGE,{"disambiguationData":[OSD([sQuery(id+"F2.wireOp",EDGE,"E195"),subQ0,sQuery(id+"F2.wireOp",EDGE,"E206")])]})});}
            var Q3;
            {var subQ0=sQuery(id+"F2.wireOp",EDGE,"E205");Q3=makeQuery(id+"F3.boolean.opBoolean","COPY",EDGE,{"disambiguationData":[topologyDisambiguationEdgeConnected([makeQuery(id+"F1.opExtrude","SWEPT_FACE",FACE,{"disambiguationData":[OSD([sQuery(id+"F0.wireOp",EDGE,"E130")])]})])],"derivedFrom":makeQuery(id+"F3.opExtrude","SWEPT_EDGE",EDGE,{"disambiguationData":[OSD([sQuery(id+"F2.wireOp",EDGE,"E195"),subQ0,sQuery(id+"F2.wireOp",EDGE,"E206")])]})});}
            var Q4;
            {var subQ0=sQuery(id+"F2.wireOp",EDGE,"E205");Q4=makeQuery(id+"F3.boolean.opBoolean","COPY",EDGE,{"disambiguationData":[topologyDisambiguationEdgeConnected([makeQuery(id+"F1.opExtrude","SWEPT_FACE",FACE,{"disambiguationData":[OSD([sQuery(id+"F0.wireOp",EDGE,"E119"),sQuery(id+"F0.wireOp",EDGE,"E193.trimOffspring")])]})])],"derivedFrom":makeQuery(id+"F3.opExtrude","SWEPT_EDGE",EDGE,{"disambiguationData":[OSD([sQuery(id+"F2.wireOp",EDGE,"E195"),subQ0,sQuery(id+"F2.wireOp",EDGE,"E206")])]})});}
            var Q5;
            {var subQ0=sQuery(id+"F2.wireOp",EDGE,"E205");Q5=makeQuery(id+"F3.boolean.opBoolean","COPY",EDGE,{"disambiguationData":[topologyDisambiguationEdgeConnected([makeQuery(id+"F1.opExtrude","SWEPT_FACE",FACE,{"disambiguationData":[OSD([sQuery(id+"F0.wireOp",EDGE,"E108"),sQuery(id+"F0.wireOp",EDGE,"E194.trimOffspring")])]})])],"derivedFrom":makeQuery(id+"F3.opExtrude","SWEPT_EDGE",EDGE,{"disambiguationData":[OSD([sQuery(id+"F2.wireOp",EDGE,"E195"),subQ0,sQuery(id+"F2.wireOp",EDGE,"E206")])]})});}
            var Q6;
            {var subQ0=sQuery(id+"F2.wireOp",EDGE,"E205");Q6=makeQuery(id+"F3.boolean.opBoolean","COPY",EDGE,{"disambiguationData":[topologyDisambiguationEdgeConnected([makeQuery(id+"F1.opExtrude","SWEPT_FACE",FACE,{"disambiguationData":[OSD([sQuery(id+"F0.wireOp",EDGE,"E97")])]})])],"derivedFrom":makeQuery(id+"F3.opExtrude","SWEPT_EDGE",EDGE,{"disambiguationData":[OSD([sQuery(id+"F2.wireOp",EDGE,"E195"),subQ0,sQuery(id+"F2.wireOp",EDGE,"E206")])]})});}
            var Q7;
            {var subQ0=sQuery(id+"F2.wireOp",EDGE,"E205");Q7=makeQuery(id+"F3.boolean.opBoolean","COPY",EDGE,{"disambiguationData":[topologyDisambiguationEdgeConnected([makeQuery(id+"F1.opExtrude","SWEPT_FACE",FACE,{"disambiguationData":[OSD([sQuery(id+"F0.wireOp",EDGE,"E86")])]})])],"derivedFrom":makeQuery(id+"F3.opExtrude","SWEPT_EDGE",EDGE,{"disambiguationData":[OSD([sQuery(id+"F2.wireOp",EDGE,"E195"),subQ0,sQuery(id+"F2.wireOp",EDGE,"E206")])]})});}
            var Q8;
            {var subQ0=sQuery(id+"F2.wireOp",EDGE,"E205");Q8=makeQuery(id+"F3.boolean.opBoolean","COPY",EDGE,{"disambiguationData":[topologyDisambiguationEdgeConnected([makeQuery(id+"F1.opExtrude","SWEPT_FACE",FACE,{"disambiguationData":[OSD([sQuery(id+"F0.wireOp",EDGE,"E75")])]})])],"derivedFrom":makeQuery(id+"F3.opExtrude","SWEPT_EDGE",EDGE,{"disambiguationData":[OSD([sQuery(id+"F2.wireOp",EDGE,"E195"),subQ0,sQuery(id+"F2.wireOp",EDGE,"E206")])]})});}
            var Q9;
            {var subQ0=sQuery(id+"F2.wireOp",EDGE,"E205");Q9=makeQuery(id+"F3.boolean.opBoolean","COPY",EDGE,{"disambiguationData":[topologyDisambiguationEdgeConnected([makeQuery(id+"F1.opExtrude","SWEPT_FACE",FACE,{"disambiguationData":[OSD([sQuery(id+"F0.wireOp",EDGE,"E64")])]})])],"derivedFrom":makeQuery(id+"F3.opExtrude","SWEPT_EDGE",EDGE,{"disambiguationData":[OSD([sQuery(id+"F2.wireOp",EDGE,"E195"),subQ0,sQuery(id+"F2.wireOp",EDGE,"E206")])]})});}
            var Q10;
            {var subQ0=sQuery(id+"F2.wireOp",EDGE,"E205");Q10=makeQuery(id+"F3.boolean.opBoolean","COPY",EDGE,{"disambiguationData":[topologyDisambiguationEdgeConnected([makeQuery(id+"F1.opExtrude","SWEPT_FACE",FACE,{"disambiguationData":[OSD([sQuery(id+"F0.wireOp",EDGE,"E54")])]})])],"derivedFrom":makeQuery(id+"F3.opExtrude","SWEPT_EDGE",EDGE,{"disambiguationData":[OSD([sQuery(id+"F2.wireOp",EDGE,"E195"),subQ0,sQuery(id+"F2.wireOp",EDGE,"E206")])]})});}
            var Q11;
            {var subQ0=sQuery(id+"F2.wireOp",EDGE,"E205");Q11=makeQuery(id+"F3.boolean.opBoolean","COPY",EDGE,{"disambiguationData":[topologyDisambiguationEdgeConnected([makeQuery(id+"F1.opExtrude","SWEPT_FACE",FACE,{"disambiguationData":[OSD([sQuery(id+"F0.wireOp",EDGE,"E40"),sQuery(id+"F0.wireOp",EDGE,"E191.trimOffspring")])]})])],"derivedFrom":makeQuery(id+"F3.opExtrude","SWEPT_EDGE",EDGE,{"disambiguationData":[OSD([sQuery(id+"F2.wireOp",EDGE,"E195"),subQ0,sQuery(id+"F2.wireOp",EDGE,"E206")])]})});}
            var Q12;
            {var subQ0=sQuery(id+"F2.wireOp",EDGE,"E205");Q12=makeQuery(id+"F3.boolean.opBoolean","COPY",EDGE,{"disambiguationData":[topologyDisambiguationEdgeConnected([makeQuery(id+"F1.opExtrude","SWEPT_FACE",FACE,{"disambiguationData":[OSD([sQuery(id+"F0.wireOp",EDGE,"E33")])]})])],"derivedFrom":makeQuery(id+"F3.opExtrude","SWEPT_EDGE",EDGE,{"disambiguationData":[OSD([sQuery(id+"F2.wireOp",EDGE,"E195"),subQ0,sQuery(id+"F2.wireOp",EDGE,"E206")])]})});}
            var Q13;
            {var subQ0=sQuery(id+"F2.wireOp",EDGE,"E205");Q13=makeQuery(id+"F3.boolean.opBoolean","COPY",EDGE,{"disambiguationData":[topologyDisambiguationEdgeConnected([makeQuery(id+"F1.opExtrude","SWEPT_FACE",FACE,{"disambiguationData":[OSD([sQuery(id+"F0.wireOp",EDGE,"E15")])]})])],"derivedFrom":makeQuery(id+"F3.opExtrude","SWEPT_EDGE",EDGE,{"disambiguationData":[OSD([sQuery(id+"F2.wireOp",EDGE,"E195"),subQ0,sQuery(id+"F2.wireOp",EDGE,"E206")])]})});}
            fillet(context, id + "F6", {"entities" : qUnion([Q0, Q1, Q2, Q3, Q4, Q5, Q6, Q7, Q8, Q9, Q10, Q11, Q12, Q13]), "radius" : 1.27 * mm, "tangentPropagation" : true, "allowEdgeOverflow" : false});
        }
        {
            var Q0;
            {var subQ2=sQuery(id+"F0.wireOp",EDGE,"E7.MirrorCS");Q0=makeQuery(id+"F3.boolean.opBoolean","SPLIT",FACE,{"disambiguationData":[TD([makeQuery(id+"F3.opExtrude","SWEPT_FACE",FACE,{"disambiguationData":[OSD([sQuery(id+"F2.wireOp",EDGE,"E203")])]})])],"derivedFrom":makeQuery(id+"F1.opExtrude","SWEPT_FACE",FACE,{"disambiguationData":[OSD([subQ2])]})});}
            var sketch = newSketch(context, id + "F7", { "sketchPlane" : qUnion([Q0])});
            skLineSegment(sketch, "E208", {"start": v(21.34, 47.63) * mm, "end": v(20.07, 47.63) * mm});
            skLineSegment(sketch, "E209", {"start": v(20.07, 47.63) * mm, "end": v(20.07, 0) * mm});
            skLineSegment(sketch, "E210", {"start": v(20.07, 0) * mm, "end": v(21.34, 0) * mm});
            skLineSegment(sketch, "E211", {"start": v(21.34, 0) * mm, "end": v(21.34, 47.63) * mm});
            skLineSegment(sketch, "E212.MirrorCS", {"start": v(-21.34, 0) * mm, "end": v(-21.34, 47.63) * mm});
            skLineSegment(sketch, "E213.MirrorCS", {"start": v(-20.07, 47.63) * mm, "end": v(-20.07, 0) * mm});
            skLineSegment(sketch, "E214.MirrorCS", {"start": v(-21.34, 47.63) * mm, "end": v(-20.07, 47.63) * mm});
            skLineSegment(sketch, "E215.MirrorCS", {"start": v(-20.07, 0) * mm, "end": v(-21.34, 0) * mm});
            skSolve(sketch);
        }
        {
            var Q0;
            Q0 = qSketchRegion(id + "F7", true);
            extrude(context, id + "F8", {"entities" : qUnion([Q0]), "operationType" : NewBodyOperationType.REMOVE, "endBound" : BoundingType.THROUGH_ALL, "oppositeDirection" : true, "depth" : 25.4 * mm});
        }
        {
            var Q0;
            {var subQ0=sQuery(id+"F7.wireOp",EDGE,"E213.MirrorCS");var subQ2=sQuery(id+"F0.wireOp",EDGE,"E9");var subQ3=sQuery(id+"F7.wireOp",EDGE,"E214.MirrorCS");Q0=makeQuery(id+"F8.boolean.opBoolean","COPY",FACE,{"disambiguationData":[TD([makeQuery(id+"F1.opExtrude","SWEPT_FACE",FACE,{"disambiguationData":[OSD([subQ2])]})])],"derivedFrom":makeQuery(id+"F8.opExtrude","CAP_FACE",FACE,{"disambiguationData":[OSD([sQuery(id+"F7.wireOp",EDGE,"E212.MirrorCS"),subQ0,subQ3,sQuery(id+"F7.wireOp",EDGE,"E215.MirrorCS")])],"isStart":true})});}
            var sketch = newSketch(context, id + "F9", { "sketchPlane" : qUnion([Q0])});
            skLineSegment(sketch, "E216", {"start": v(20.07, 47.63) * mm, "end": v(20.07, 0) * mm});
            skLineSegment(sketch, "E217", {"start": v(20.07, 0) * mm, "end": v(21.34, 0) * mm});
            skLineSegment(sketch, "E218", {"start": v(21.34, 0) * mm, "end": v(21.34, 47.63) * mm});
            skLineSegment(sketch, "E219", {"start": v(21.34, 47.63) * mm, "end": v(20.07, 47.63) * mm});
            skLineSegment(sketch, "E220.MirrorCS", {"start": v(-20.07, 47.63) * mm, "end": v(-20.07, 0) * mm});
            skLineSegment(sketch, "E221.MirrorCS", {"start": v(-21.34, 0) * mm, "end": v(-21.34, 47.63) * mm});
            skLineSegment(sketch, "E222.MirrorCS", {"start": v(-21.34, 47.63) * mm, "end": v(-20.07, 47.63) * mm});
            skLineSegment(sketch, "E223.MirrorCS", {"start": v(-20.07, 0) * mm, "end": v(-21.34, 0) * mm});
            skSolve(sketch);
        }
        {
            var Q0;
            Q0 = qSketchRegion(id + "F9", true);
            extrude(context, id + "F10", {"entities" : qUnion([Q0]), "operationType" : NewBodyOperationType.REMOVE, "endBound" : BoundingType.THROUGH_ALL, "oppositeDirection" : true, "depth" : 25.4 * mm});
        }
        {
            var Q0;
            {var subQ2=sQuery(id+"F0.wireOp",EDGE,"E6.MirrorCS");Q0=makeQuery(id+"F3.boolean.opBoolean","SPLIT",FACE,{"disambiguationData":[TD([makeQuery(id+"F3.opExtrude","SWEPT_FACE",FACE,{"disambiguationData":[OSD([sQuery(id+"F2.wireOp",EDGE,"E203")])]})])],"derivedFrom":makeQuery(id+"F1.opExtrude","SWEPT_FACE",FACE,{"disambiguationData":[OSD([subQ2])]})});}
            var sketch = newSketch(context, id + "F11", { "sketchPlane" : qUnion([Q0])});
            skLineSegment(sketch, "E224", {"start": v(21.34, 47.63) * mm, "end": v(17.32, 50.8) * mm});
            skLineSegment(sketch, "E225", {"start": v(17.32, 50.8) * mm, "end": v(21.34, 50.8) * mm});
            skLineSegment(sketch, "E226", {"start": v(21.34, 50.8) * mm, "end": v(21.34, 47.63) * mm});
            skLineSegment(sketch, "E227.MirrorCS", {"start": v(-17.32, 50.8) * mm, "end": v(-21.34, 50.8) * mm});
            skLineSegment(sketch, "E228.MirrorCS", {"start": v(-21.34, 47.63) * mm, "end": v(-17.32, 50.8) * mm});
            skLineSegment(sketch, "E229.MirrorCS", {"start": v(-21.34, 50.8) * mm, "end": v(-21.34, 47.63) * mm});
            skSolve(sketch);
        }
        {
            var Q0;
            Q0 = qSketchRegion(id + "F11", true);
            extrude(context, id + "F12", {"entities" : qUnion([Q0]), "operationType" : NewBodyOperationType.REMOVE, "endBound" : BoundingType.THROUGH_ALL, "oppositeDirection" : true, "depth" : 25.4 * mm});
        }
    });
